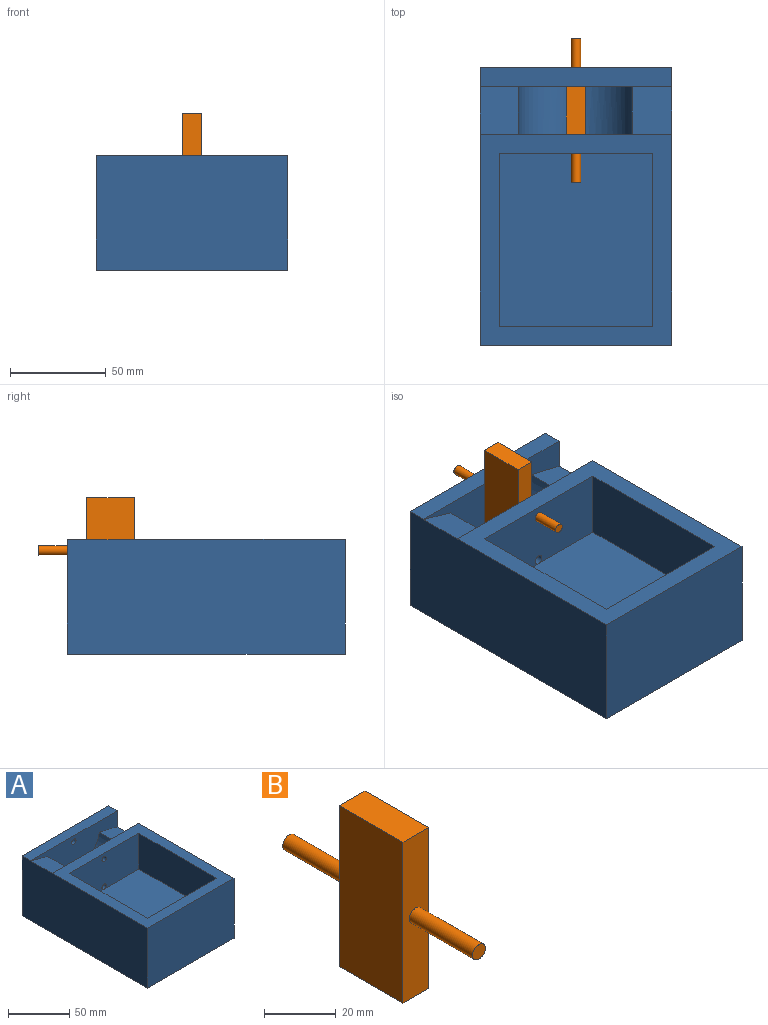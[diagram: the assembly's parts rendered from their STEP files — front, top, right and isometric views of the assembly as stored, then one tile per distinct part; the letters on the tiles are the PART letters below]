
ASSEMBLY  parts=2 mates=1
PART A: 20 faces, bbox 100x145x60 mm
  f0: cylinder r=2.5mm len=10mm, axis (0,-1,0), area 157.1mm2, adj f11,f16,f17
  f1: plane 80x35.82mm, normal (0,1,0), area 2865.6mm2, adj f2,f16,f18,f19
  f2: plane 110x100mm, normal (0,0,1), area 3800mm2, adj f1,f5,f7,f11,f15,f17,f18,f19
  f3: cylinder r=2.5mm len=10mm, axis (0,1,0), area 157.1mm2, adj f11,f17
  f4: plane 100x10mm, normal (0,0,1), area 1000mm2, adj f5,f7,f9,f10
  f5: plane 145x60mm, normal (1,0,0), area 8297.5mm2, adj f2,f4,f8,f9,f10,f11,f14,f15
  f6: cylinder r=30mm len=59.51mm, axis (0,1,0), area 2220.8mm2, adj f9,f11,f13,f14
  f7: plane 145x60mm, normal (-1,0,0), area 8696.2mm2, adj f2,f4,f8,f9,f10,f11,f13,f15
  f8: plane 145x100mm, normal (0,0,-1), area 14500mm2, adj f5,f7,f10,f15
  f9: plane 100x35.82mm, normal (0,-1,0), area 2079.4mm2, adj f4,f5,f6,f7,f12,f13,f14
  f10: plane 100x60mm, normal (0,1,0), area 5980.4mm2, adj f4,f5,f7,f8,f12
  f11: plane 100x35.82mm, normal (0,1,0), area 2059.8mm2, adj f0,f2,f3,f5,f6,f7,f13,f14
  f12: cylinder r=2.5mm len=10mm, axis (0,1,0), area 157.1mm2, adj f9,f10
  f13: plane 25x19.91mm, normal (0.27,0,0.96), area 517.6mm2, adj f6,f7,f9,f11
  f14: plane 25x20.58mm, normal (0.23,0,0.97), area 528.8mm2, adj f5,f6,f9,f11
  f15: plane 100x60mm, normal (0,-1,0), area 6000mm2, adj f2,f5,f7,f8
  f16: plane 90.01x80.01mm, normal (0,0,1), area 7200mm2, adj f0,f1,f17,f18,f19
  f17: plane 80x35.82mm, normal (0,-1,0), area 2826.3mm2, adj f0,f2,f3,f16,f18,f19
  f18: plane 90x35.82mm, normal (1,0,0), area 3223.8mm2, adj f1,f2,f16,f17
  f19: plane 90x35.82mm, normal (-1,0,0), area 3223.8mm2, adj f1,f2,f16,f17
PART B: 10 faces, bbox 10x75x55 mm
  f0: plane 25x10mm, normal (0,0,1), area 250mm2, adj f2,f3,f4,f7
  f1: plane 25x10mm, normal (0,0,-1), area 250mm2, adj f2,f3,f4,f7
  f2: plane 55x25mm, normal (1,0,0), area 1375mm2, adj f0,f1,f4,f7
  f3: plane 55x25mm, normal (-1,0,0), area 1375mm2, adj f0,f1,f4,f7
  f4: plane 55x10mm, normal (0,1,0), area 530.4mm2, adj f0,f1,f2,f3,f5
  f5: cylinder r=2.5mm len=25mm, axis (0,-1,0), area 392.7mm2, adj f4,f6
  f6: plane 5x5mm, normal (0,1,0), area 19.6mm2, adj f5
  f7: plane 55x10mm, normal (0,-1,0), area 530.4mm2, adj f0,f1,f2,f3,f8
  f8: cylinder r=2.5mm len=25mm, axis (0,1,0), area 392.7mm2, adj f7,f9
  f9: plane 5x5mm, normal (0,-1,0), area 19.6mm2, adj f8
PLACE A t=(38.33,1.18,42.44)mm
PLACE B t=(38.44,1.18,41.09)mm
MATE revolute B.f5 <-> A.f3  axis (0,1,0) through (38.33,26.18,42.44)mm
